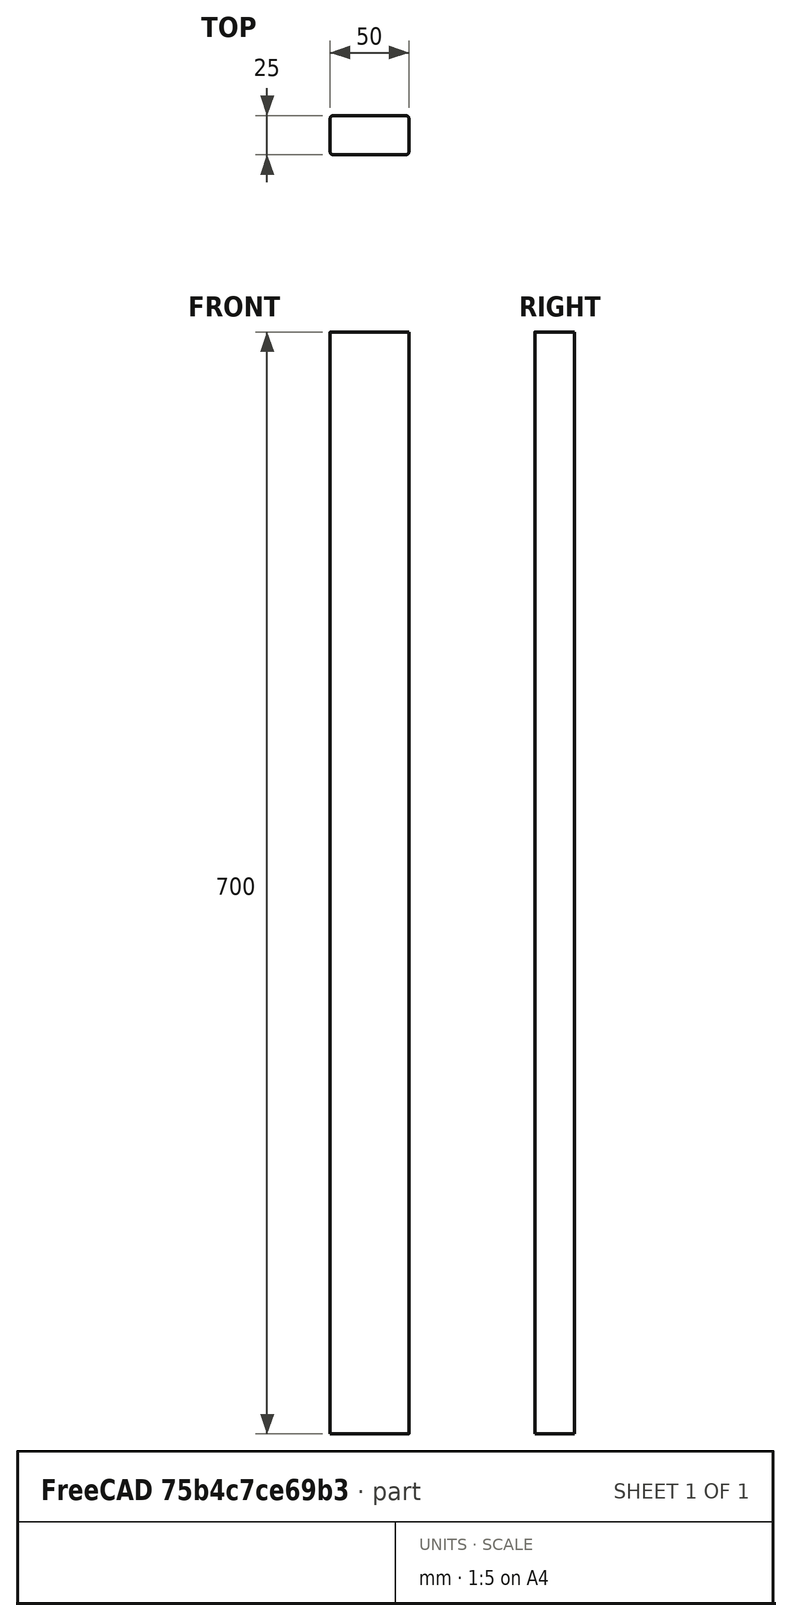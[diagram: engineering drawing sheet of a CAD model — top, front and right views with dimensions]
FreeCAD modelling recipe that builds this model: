
FCSTD DOCUMENT  (FreeCAD 0.19R)
Label: column_50_25
License: All rights reserved
LicenseURL: http://en.wikipedia.org/wiki/All_rights_reserved
objects: PartDesign::CoordinateSystem×4, Sketcher::SketchObject×1, PartDesign::Pad×1, PartDesign::Body×1
note: 8 computed .brp shape members not serialized (recipe doc carries the construction recipe); baked Part::Feature solids carry a one-line shape summary decoded from their .brp

FEATURE [PartDesign::CoordinateSystem] LCS_0
  AttacherType = Attacher::AttachEngine3D
  MapMode = 2
  Support = -> [X_Axis]
FEATURE [Sketcher::SketchObject] Sketch
  FullyConstrained = true
  MapMode = 5
  Support = -> [XY_Plane]
  sketch-geometry (8):
    g0: LineSegment StartX=-23 StartY=12.5 StartZ=0 EndX=23 EndY=12.5 EndZ=0
    g1: LineSegment StartX=25 StartY=10.5 StartZ=0 EndX=25 EndY=-10.5 EndZ=0
    g2: LineSegment StartX=23 StartY=-12.5 StartZ=0 EndX=-23 EndY=-12.5 EndZ=0
    g3: LineSegment StartX=-25 StartY=-10.5 StartZ=0 EndX=-25 EndY=10.5 EndZ=0
    g4: ArcOfCircle CenterX=-23 CenterY=10.5 CenterZ=0 NormalX=0 NormalY=0 NormalZ=1 AngleXU=0 Radius=2 StartAngle=1.5708 EndAngle=3.14159
    g5: ArcOfCircle CenterX=-23 CenterY=-10.5 CenterZ=0 NormalX=0 NormalY=0 NormalZ=1 AngleXU=0 Radius=2 StartAngle=3.14159 EndAngle=4.71239
    g6: ArcOfCircle CenterX=23 CenterY=-10.5 CenterZ=0 NormalX=0 NormalY=0 NormalZ=1 AngleXU=0 Radius=2 StartAngle=4.71239 EndAngle=6.28319
    g7: ArcOfCircle CenterX=23 CenterY=10.5 CenterZ=0 NormalX=0 NormalY=0 NormalZ=1 AngleXU=0 Radius=2 StartAngle=0 EndAngle=1.5708
  constraints (18):
    c: Horizontal(g0)
    c: Horizontal(g2)
    c: Vertical(g1)
    c: Vertical(g3)
    c: Tangent(g3,g4) = 1.5708
    c: Tangent(g0,g4) = 1.5708
    c: Tangent(g2,g5) = 1.5708
    c: Tangent(g3,g5) = 1.5708
    c: Tangent(g1,g6) = 1.5708
    c: Tangent(g2,g6) = 1.5708
    c: Tangent(g0,g7) = 1.5708
    c: Tangent(g1,g7) = 1.5708
    c: Radius(g4) = 2
    c: Equal(g4,g7)
    c: DistanceY(g2,g0) = 25
    c: DistanceX(g3,g1) = 50
    c: Symmetric(g2,g0,g-1)
    c: Symmetric(g3,g1,g-2)
FEATURE [PartDesign::Pad] Pad
  Direction = (1,1,1)
  Length = 700
  Length2 = 100
  Profile = -> Sketch
  Type = 0
FEATURE [PartDesign::CoordinateSystem] LCS_bottom
  AttacherType = Attacher::AttachEngine3D
  AttachmentOffset = pos=(0,25,0) rot=(0,0,1;0rad)
  MapMode = 5
  Placement = pos=(0,-12.5,25) rot=(1,0,0;1.5708rad)
  Support = -> [Pad]
FEATURE [PartDesign::CoordinateSystem] LCS_bottom_narrow1
  AttacherType = Attacher::AttachEngine3D
  AttachmentOffset = pos=(0,25,0) rot=(0,0,1;0rad)
  MapMode = 5
  Placement = pos=(25,0,25) rot=(0.57735,0.57735,0.57735;2.0944rad)
  Support = -> [Pad]
FEATURE [PartDesign::CoordinateSystem] LCS_bottom_narrow_2
  AttacherType = Attacher::AttachEngine3D
  AttachmentOffset = pos=(0,25,0) rot=(0,0,1;0rad)
  MapMode = 5
  Placement = pos=(-25,0,25) rot=(0.57735,-0.57735,-0.57735;2.0944rad)
  Support = -> [Pad]
FEATURE [PartDesign::Body] SmallColumnBody
  Group = -> [LCS_0,Sketch,Pad,LCS_bottom,LCS_bottom_narrow1,LCS_bottom_narrow_2]
  Origin = -> Origin
  Tip = -> Pad
